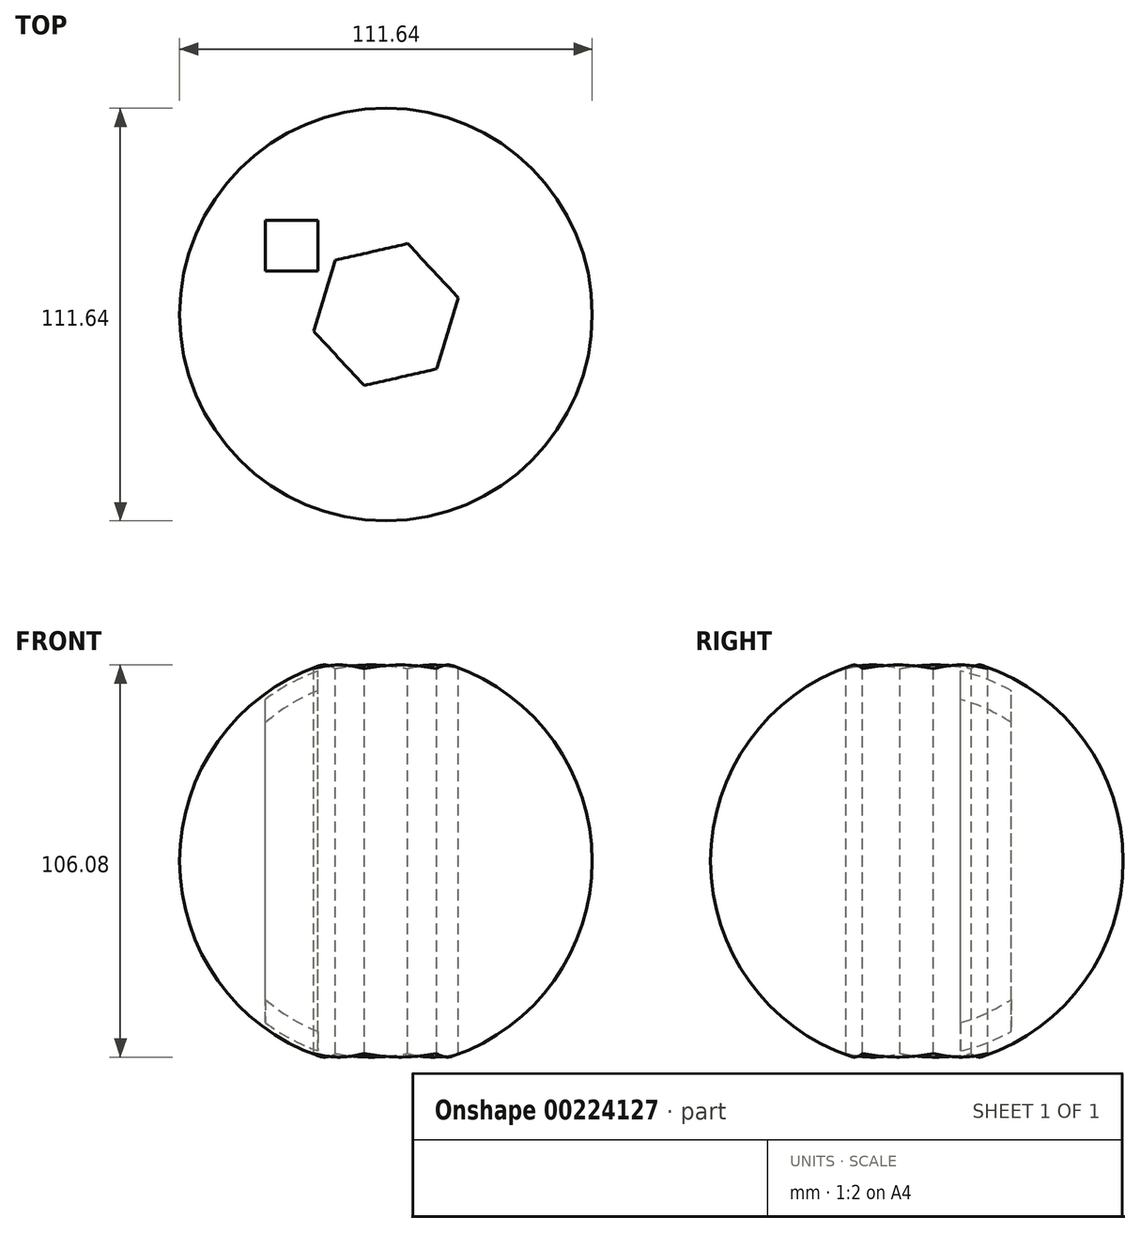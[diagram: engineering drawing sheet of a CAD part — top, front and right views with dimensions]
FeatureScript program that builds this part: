
annotation { "Feature Type Name" : "Feature", "Feature Type Description" : "" }
export const myFeature = defineFeature(function(context is Context, id is Id, definition is map)
    precondition{}
    {
        {
            var Q0;
            Q0=qCreatedBy(makeId("Front.planeOp"),FACE);
            var sketch = newSketch(context, id + "F0", { "sketchPlane" : qUnion([Q0])});
            skLineSegment(sketch, "E0", {"start": v(0, 56.1) * mm, "end": v(0, -55.82) * mm});
            skCircle(sketch, "E1", {"center": v(0, 0) * mm, "radius": 55.82 * mm});
            skSolve(sketch);
        }
        {
            var Q0;
            {var subQ0=sQuery(id+"F0.wireOp",EDGE,"E1");var subQ1=sQuery(id+"F0.wireOp",EDGE,"E0");var subQ2=makeQuery(id+"F0.imprint","INTERSECT",VERTEX,{"disambiguationData":[OD(0.0)],"derivedFrom":[subQ1,subQ0]});Q0=makeQuery(id+"F0.imprint","IMPRINT",FACE,{"disambiguationData":[TD([[makeQuery(id+"F0.imprint","IMPRINT",EDGE,{"disambiguationData":[TD([[subQ2,1.0]])],"derivedFrom":subQ1}),-1.0]])]});}
            var Q1;
            Q1=sQuery(id+"F0.wireOp",EDGE,"E0");
            revolve(context, id + "F1", {"entities" : qUnion([Q0]), "axis" : qUnion([Q1]), "revolveType" : RevolveType.FULL});
        }
        {
            var Q0;
            Q0=qCreatedBy(makeId("Top.planeOp"),FACE);
            var sketch = newSketch(context, id + "F2", { "sketchPlane" : qUnion([Q0])});
            skLineSegment(sketch, "E2.bottom", {"start": v(-32.65, 25.5) * mm, "end": v(-18.36, 25.5) * mm});
            skLineSegment(sketch, "E2.top", {"start": v(-32.65, 11.8) * mm, "end": v(-18.36, 11.8) * mm});
            skLineSegment(sketch, "E2.left", {"start": v(-32.65, 25.5) * mm, "end": v(-32.65, 11.8) * mm});
            skLineSegment(sketch, "E2.right", {"start": v(-18.36, 25.5) * mm, "end": v(-18.36, 11.8) * mm});
            skSolve(sketch);
        }
        {
            var Q0;
            Q0 = qSketchRegion(id + "F2", true);
            extrude(context, id + "F3", {"entities" : qUnion([Q0]), "operationType" : NewBodyOperationType.REMOVE, "oppositeDirection" : true, "depth" : 67.82 * mm});
        }
        {
            var Q0;
            Q0 = qSketchRegion(id + "F2", true);
            extrude(context, id + "F4", {"entities" : qUnion([Q0]), "operationType" : NewBodyOperationType.REMOVE, "depth" : 222 * mm});
        }
        {
            var Q0;
            Q0=qCreatedBy(makeId("Top.planeOp"),FACE);
            var sketch = newSketch(context, id + "F5", { "sketchPlane" : qUnion([Q0])});
            skCircle(sketch, "E3.cCircle", {"center": v(0, 0) * mm, "radius": 17.4 * mm, "construction": true});
            skLineSegment(sketch, "E3.0", {"start": v(5.89, 19.2) * mm, "end": v(19.58, 4.5) * mm});
            skLineSegment(sketch, "E3.1", {"start": v(19.58, 4.5) * mm, "end": v(13.7, -14.7) * mm});
            skLineSegment(sketch, "E3.2", {"start": v(13.7, -14.7) * mm, "end": v(-5.89, -19.2) * mm});
            skLineSegment(sketch, "E3.3", {"start": v(-5.89, -19.2) * mm, "end": v(-19.58, -4.5) * mm});
            skLineSegment(sketch, "E3.4", {"start": v(-19.58, -4.5) * mm, "end": v(-13.7, 14.7) * mm});
            skLineSegment(sketch, "E3.5", {"start": v(-13.7, 14.7) * mm, "end": v(5.89, 19.2) * mm});
            skPoint(sketch, "E3.0.midPoint", {"position": v(12.73, 11.86) * mm});
            skSolve(sketch);
        }
        {
            var Q0;
            Q0 = qSketchRegion(id + "F5", true);
            extrude(context, id + "F6", {"entities" : qUnion([Q0]), "operationType" : NewBodyOperationType.REMOVE, "oppositeDirection" : true, "depth" : 96.77 * mm});
        }
        {
            var Q0;
            Q0=makeQuery(id+"F6.boolean.opBoolean","COPY",FACE,{"derivedFrom":makeQuery(id+"F6.opExtrude","CAP_FACE",FACE,{"disambiguationData":[OSD([sQuery(id+"F5.wireOp",EDGE,"E3.0"),sQuery(id+"F5.wireOp",EDGE,"E3.1"),sQuery(id+"F5.wireOp",EDGE,"E3.2"),sQuery(id+"F5.wireOp",EDGE,"E3.3"),sQuery(id+"F5.wireOp",EDGE,"E3.4"),sQuery(id+"F5.wireOp",EDGE,"E3.5")])],"isStart":true})});
            extrude(context, id + "F7", {"entities" : qUnion([Q0]), "operationType" : NewBodyOperationType.REMOVE, "oppositeDirection" : true, "depth" : 104.65 * mm});
        }
    });
